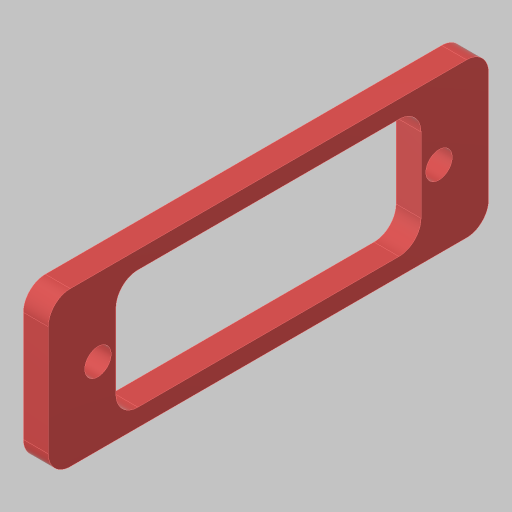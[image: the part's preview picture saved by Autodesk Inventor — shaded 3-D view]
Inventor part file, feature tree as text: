
AUTODESK INVENTOR PART (.ipt)
format: ipt  version: 2023.5 (Build 275446000, 446)  size: 133,120 bytes
history: native  units: in
note: dims shown in document units (in); Inventor stores cm internally (conversion verified against a paired STEP export)
features: extrude x2, sketch x2, hole x1, fillet x1
ambient origin geometry x8: Origin, YZ Plane, XZ Plane, XY Plane, X Axis, Y Axis, Z Axis, Center Point
bodies: Solid1 (feature_tree)
feature tree (6):
  extrude  "Extrusion1"  Depth=0.875in
  sketch  "Sketch2"  dims[d2=0.1417in d3=0.0in d4=1.7323in d5=0.675in d7=0.2362in d8=0.1417in d9=0.0in d10=0.15in d11=0.75in d12=0.279in d13=0.25in d14=0.5635in d15=1.0in d16=0.8108in d20=1.9366in d21=0.125in]
  extrude  "Extrusion2"  Depth=1.7323in
  hole  "Hole1"  [1 undecoded]
  fillet  "Fillet1"  Radius=0.2362in
  sketch  "Sketch1"  dims[d0=2.5in d1=0.875in]
note: 1 required parameter value undecoded (feature->parameter linkage not recoverable at this tier; creation-order binding heuristic only, values carry confidence <= 0.55)
